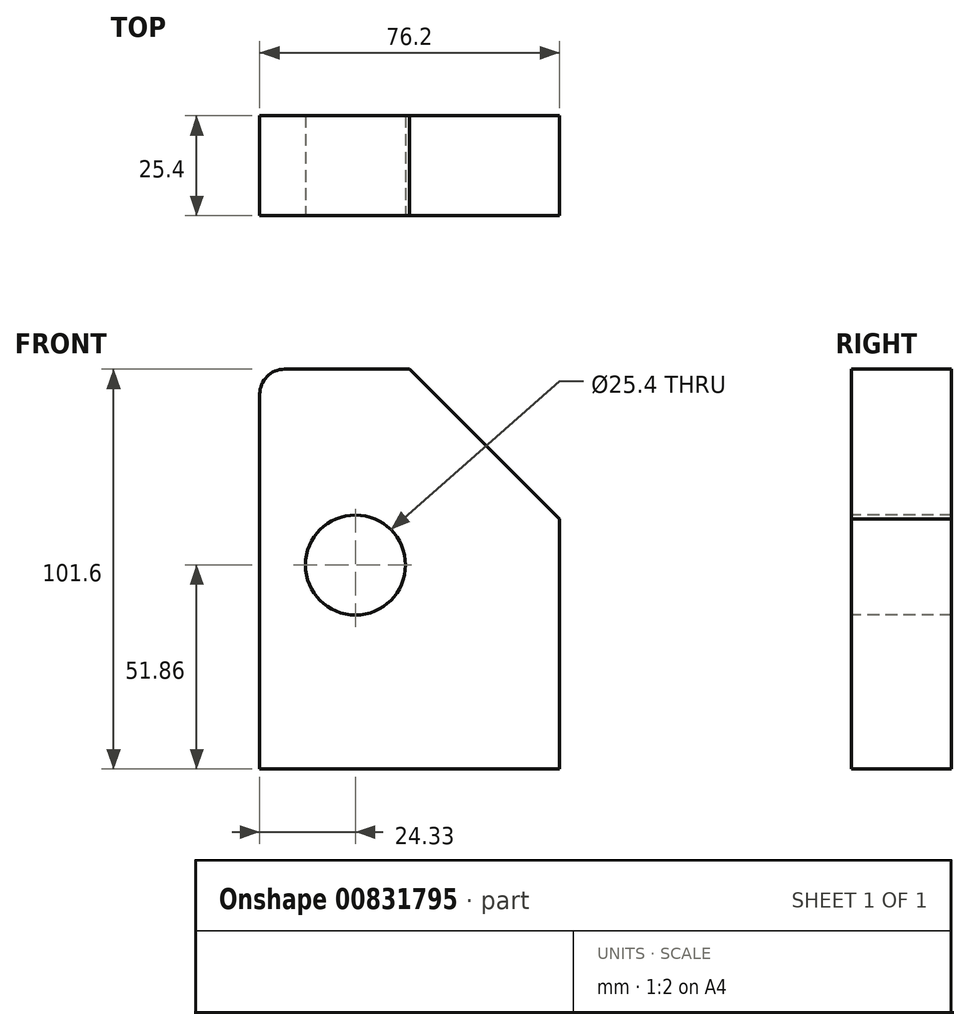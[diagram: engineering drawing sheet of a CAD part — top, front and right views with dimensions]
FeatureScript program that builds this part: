
annotation { "Feature Type Name" : "Feature", "Feature Type Description" : "" }
export const myFeature = defineFeature(function(context is Context, id is Id, definition is map)
    precondition{}
    {
        {
            var Q0;
            Q0=qCreatedBy(makeId("Front.planeOp"),FACE);
            var sketch = newSketch(context, id + "F0", { "sketchPlane" : qUnion([Q0])});
            skLineSegment(sketch, "E0.bottom", {"start": v(-32.63, 61.76) * mm, "end": v(37.22, 61.76) * mm});
            skLineSegment(sketch, "E0.top", {"start": v(-38.98, -39.84) * mm, "end": v(37.22, -39.84) * mm});
            skLineSegment(sketch, "E0.left", {"start": v(-38.98, 55.41) * mm, "end": v(-38.98, -39.84) * mm});
            skLineSegment(sketch, "E0.right", {"start": v(37.22, 61.76) * mm, "end": v(37.22, -39.84) * mm});
            skPoint(sketch, "E1.visualSharp", {"position": v(-38.98, 61.76) * mm});
            skArc(sketch, "E1.filletArc", {"start": v(-32.63, 61.76) * mm, "mid": v(-37.12, 59.9) * mm, "end": v(-38.98, 55.41) * mm});
            skSolve(sketch);
        }
        {
            var Q0;
            Q0=makeQuery(id+"F0.imprint","IMPRINT",FACE,{"disambiguationData":[TD([[makeQuery(id+"F0.imprint","IMPRINT",EDGE,{"derivedFrom":sQuery(id+"F0.wireOp",EDGE,"E0.bottom")}),-1.0]])]});
            extrude(context, id + "F1", {"entities" : qUnion([Q0]), "depth" : 25.4 * mm, "offsetDistance" : 25.4 * mm});
        }
        {
            var Q0;
            Q0=makeQuery(id+"F1.opExtrude","SWEPT_EDGE",EDGE,{"disambiguationData":[OSD([sQuery(id+"F0.wireOp",EDGE,"E0.bottom"),sQuery(id+"F0.wireOp",EDGE,"E0.right")])]});
            chamfer(context, id + "F2", {"entities" : qUnion([Q0]), "width" : 38.1 * mm, "tangentPropagation" : true});
        }
        {
            var Q0;
            Q0=makeQuery(id+"F1.opExtrude","CAP_FACE",FACE,{"disambiguationData":[OSD([sQuery(id+"F0.wireOp",EDGE,"E0.bottom"),sQuery(id+"F0.wireOp",EDGE,"E0.top"),sQuery(id+"F0.wireOp",EDGE,"E0.left"),sQuery(id+"F0.wireOp",EDGE,"E0.right"),sQuery(id+"F0.wireOp",EDGE,"E1.filletArc")])],"isStart":false});
            var sketch = newSketch(context, id + "F3", { "sketchPlane" : qUnion([Q0])});
            skCircle(sketch, "E2", {"center": v(-14.65, 12.02) * mm, "radius": 12.7 * mm});
            skSolve(sketch);
        }
        {
            var Q0;
            Q0 = qSketchRegion(id + "F3", true);
            extrude(context, id + "F4", {"entities" : qUnion([Q0]), "operationType" : NewBodyOperationType.REMOVE, "oppositeDirection" : true, "depth" : 86.61 * mm, "offsetDistance" : 25.4 * mm});
        }
    });
